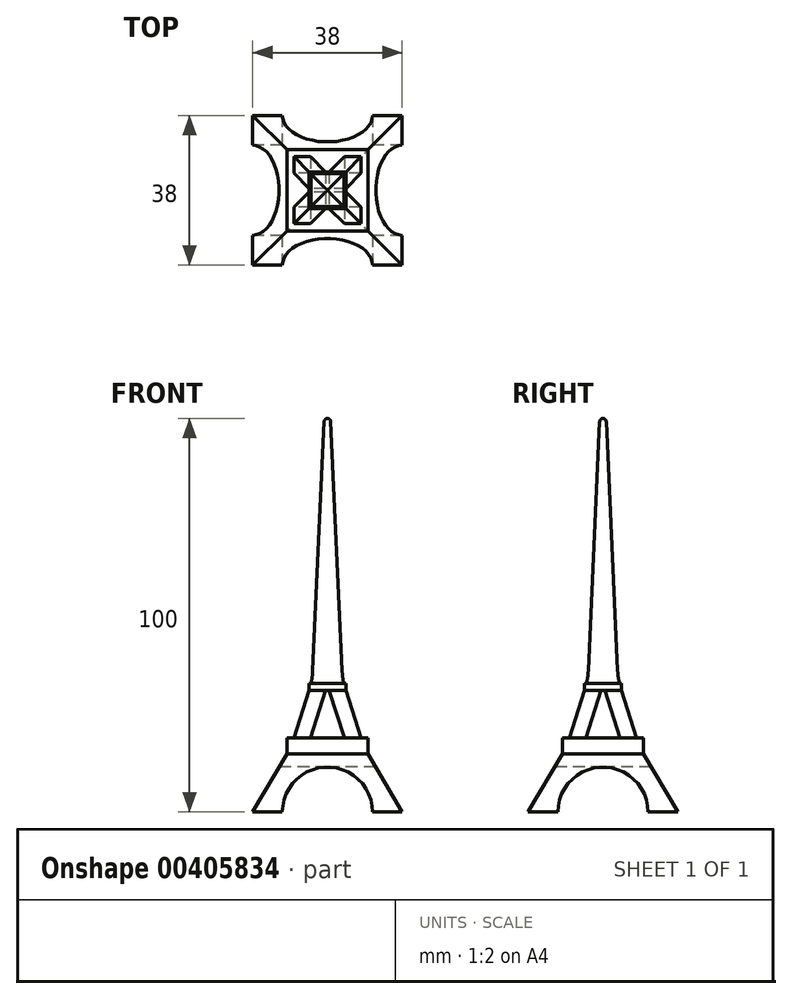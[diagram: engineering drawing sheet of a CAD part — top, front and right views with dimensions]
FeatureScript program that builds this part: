
annotation { "Feature Type Name" : "Feature", "Feature Type Description" : "" }
export const myFeature = defineFeature(function(context is Context, id is Id, definition is map)
    precondition{}
    {
        {
            var Q0;
            Q0=qCreatedBy(makeId("Front.planeOp"),FACE);
            var sketch = newSketch(context, id + "F0", { "sketchPlane" : qUnion([Q0])});
            skLineSegment(sketch, "E0.bottom", {"start": v(0, 0) * mm, "end": v(38, 0) * mm});
            skLineSegment(sketch, "E0.top", {"start": v(0, 100) * mm, "end": v(38, 100) * mm});
            skLineSegment(sketch, "E0.left", {"start": v(0, 0) * mm, "end": v(0, 100) * mm});
            skLineSegment(sketch, "E0.right", {"start": v(38, 0) * mm, "end": v(38, 100) * mm});
            skSolve(sketch);
        }
        {
            var Q0;
            Q0=makeQuery(id+"F0.imprint","IMPRINT",FACE,{"disambiguationData":[TD([[makeQuery(id+"F0.imprint","IMPRINT",EDGE,{"derivedFrom":sQuery(id+"F0.wireOp",EDGE,"E0.bottom")}),1.0]])]});
            extrude(context, id + "F1", {"entities" : qUnion([Q0]), "depth" : 38 * mm});
        }
        {
            var Q0;
            Q0=makeQuery(id+"F1.opExtrude","CAP_FACE",FACE,{"disambiguationData":[OSD([sQuery(id+"F0.wireOp",EDGE,"E0.bottom"),sQuery(id+"F0.wireOp",EDGE,"E0.top"),sQuery(id+"F0.wireOp",EDGE,"E0.left"),sQuery(id+"F0.wireOp",EDGE,"E0.right")])],"isStart":false});
            var sketch = newSketch(context, id + "F2", { "sketchPlane" : qUnion([Q0])});
            skPoint(sketch, "E1.endSnap0", {"position": v(19, 100) * mm});
            skLineSegment(sketch, "E2", {"start": v(19, 100) * mm, "end": v(19, 0) * mm, "construction": true});
            skLineSegment(sketch, "E3", {"start": v(19, 100) * mm, "end": v(19.03, 100) * mm});
            skLineSegment(sketch, "E4", {"start": v(19.83, 99.24) * mm, "end": v(22.72, 36.04) * mm});
            skLineSegment(sketch, "E5", {"start": v(38, 0) * mm, "end": v(29.32, 14.77) * mm});
            skLineSegment(sketch, "E6", {"start": v(27.53, 18.8) * mm, "end": v(23.66, 30.85) * mm});
            skArc(sketch, "E7", {"start": v(30.49, 0) * mm, "mid": v(27.12, 8.12) * mm, "end": v(19, 11.49) * mm});
            skLineSegment(sketch, "E8", {"start": v(38, 0) * mm, "end": v(30.49, 0) * mm});
            skPoint(sketch, "E9.visualSharp", {"position": v(22.85, 33.38) * mm});
            skArc(sketch, "E9.filletArc", {"start": v(22.72, 36.04) * mm, "mid": v(22.88, 34.33) * mm, "end": v(23.17, 32.64) * mm});
            skPoint(sketch, "E10.visualSharp", {"position": v(28.2, 16.68) * mm});
            skLineSegment(sketch, "E11.MirrorCS", {"start": v(18.17, 99.24) * mm, "end": v(15.28, 36.04) * mm});
            skArc(sketch, "E12.MirrorCS", {"start": v(15.28, 36.04) * mm, "mid": v(15.12, 34.33) * mm, "end": v(14.83, 32.64) * mm});
            skLineSegment(sketch, "E13.MirrorCS", {"start": v(10.47, 18.8) * mm, "end": v(14.34, 30.85) * mm});
            skLineSegment(sketch, "E14.MirrorCS", {"start": v(19, 100) * mm, "end": v(18.97, 100) * mm});
            skLineSegment(sketch, "E15.MirrorCS", {"start": v(0, 0) * mm, "end": v(8.68, 14.77) * mm});
            skArc(sketch, "E16.MirrorCS", {"start": v(7.51, 0) * mm, "mid": v(10.88, 8.12) * mm, "end": v(19, 11.49) * mm});
            skLineSegment(sketch, "E17.MirrorCS", {"start": v(0, 0) * mm, "end": v(7.51, 0) * mm});
            skLineSegment(sketch, "E18.bottom", {"start": v(-8.57, -4.89) * mm, "end": v(50.47, -4.89) * mm});
            skLineSegment(sketch, "E18.top", {"start": v(-8.57, 109.12) * mm, "end": v(50.47, 109.12) * mm});
            skLineSegment(sketch, "E18.left", {"start": v(-8.57, -4.89) * mm, "end": v(-8.57, 109.12) * mm});
            skLineSegment(sketch, "E18.right", {"start": v(50.47, -4.89) * mm, "end": v(50.47, 109.12) * mm});
            skLineSegment(sketch, "E19", {"start": v(29.32, 14.77) * mm, "end": v(29.32, 18.8) * mm});
            skLineSegment(sketch, "E20", {"start": v(29.32, 18.8) * mm, "end": v(27.53, 18.8) * mm});
            skLineSegment(sketch, "E21.MirrorCS", {"start": v(8.68, 18.8) * mm, "end": v(10.47, 18.8) * mm});
            skLineSegment(sketch, "E22.MirrorCS", {"start": v(8.68, 14.77) * mm, "end": v(8.68, 18.8) * mm});
            skLineSegment(sketch, "E23", {"start": v(23.66, 30.85) * mm, "end": v(23.66, 32.64) * mm});
            skLineSegment(sketch, "E24", {"start": v(23.66, 32.64) * mm, "end": v(23.17, 32.64) * mm});
            skLineSegment(sketch, "E25.MirrorCS", {"start": v(14.34, 30.85) * mm, "end": v(14.34, 32.64) * mm});
            skLineSegment(sketch, "E26.MirrorCS", {"start": v(14.34, 32.64) * mm, "end": v(14.83, 32.64) * mm});
            skPoint(sketch, "E27.orphan", {"position": v(14.34, 30.85) * mm});
            skPoint(sketch, "E28.visualSharp", {"position": v(18.2, 100) * mm});
            skArc(sketch, "E28.filletArc", {"start": v(18.97, 100) * mm, "mid": v(18.42, 99.78) * mm, "end": v(18.17, 99.24) * mm});
            skPoint(sketch, "E29.visualSharp", {"position": v(19.8, 100) * mm});
            skArc(sketch, "E29.filletArc", {"start": v(19.83, 99.24) * mm, "mid": v(19.58, 99.78) * mm, "end": v(19.03, 100) * mm});
            skLineSegment(sketch, "E30.0", {"start": v(14.67, 18.8) * mm, "end": v(18.54, 30.85) * mm});
            skLineSegment(sketch, "E31.0", {"start": v(23.33, 18.8) * mm, "end": v(19.46, 30.85) * mm});
            skLineSegment(sketch, "E32", {"start": v(23.33, 18.8) * mm, "end": v(14.67, 18.8) * mm});
            skLineSegment(sketch, "E33", {"start": v(19.46, 30.85) * mm, "end": v(18.54, 30.85) * mm});
            skSolve(sketch);
        }
        {
            var Q0;
            {var subQ2=sQuery(id+"F2.wireOp",EDGE,"E11.MirrorCS");Q0=makeQuery(id+"F2.imprint","IMPRINT",FACE,{"disambiguationData":[TD([[makeQuery(id+"F2.imprint","IMPRINT",EDGE,{"derivedFrom":subQ2}),-1.0]])]});}
            var Q1;
            {var subQ0=sQuery(id+"F2.wireOp",EDGE,"E7");Q1=makeQuery(id+"F2.imprint","IMPRINT",FACE,{"disambiguationData":[TD([[makeQuery(id+"F2.imprint","IMPRINT",EDGE,{"derivedFrom":subQ0}),1.0]])]});}
            var Q2;
            {var subQ2=sQuery(id+"F2.wireOp",EDGE,"E4");Q2=makeQuery(id+"F2.imprint","IMPRINT",FACE,{"disambiguationData":[TD([[makeQuery(id+"F2.imprint","IMPRINT",EDGE,{"derivedFrom":subQ2}),1.0]])]});}
            var Q3;
            Q3=makeQuery(id+"F2.imprint","IMPRINT",FACE,{"disambiguationData":[TD([[makeQuery(id+"F2.imprint","IMPRINT",EDGE,{"derivedFrom":sQuery(id+"F2.wireOp",EDGE,"E30.0")}),-1.0]])]});
            extrude(context, id + "F3", {"entities" : qUnion([Q0, Q1, Q2, Q3]), "operationType" : NewBodyOperationType.REMOVE, "endBound" : BoundingType.THROUGH_ALL, "oppositeDirection" : true, "depth" : 25 * mm});
        }
        {
            var Q0;
            Q0=qCreatedBy(makeId("Right.planeOp"),FACE);
            var sketch = newSketch(context, id + "F4", { "sketchPlane" : qUnion([Q0])});
            skPoint(sketch, "E34.endSnap0", {"position": v(-19, 100) * mm});
            skLineSegment(sketch, "E35", {"start": v(-19, 100) * mm, "end": v(-19, 0) * mm, "construction": true});
            skLineSegment(sketch, "E36", {"start": v(-19, 100) * mm, "end": v(-18.97, 100) * mm});
            skLineSegment(sketch, "E37", {"start": v(-18.17, 99.24) * mm, "end": v(-15.28, 36.04) * mm});
            skLineSegment(sketch, "E38", {"start": v(0, 0) * mm, "end": v(-8.68, 14.77) * mm});
            skLineSegment(sketch, "E39", {"start": v(-10.47, 18.8) * mm, "end": v(-14.34, 30.85) * mm});
            skArc(sketch, "E40", {"start": v(-7.51, 0) * mm, "mid": v(-10.88, 8.12) * mm, "end": v(-19, 11.49) * mm});
            skLineSegment(sketch, "E41", {"start": v(0, 0) * mm, "end": v(-7.51, 0) * mm});
            skPoint(sketch, "E42.visualSharp", {"position": v(-15.15, 33.38) * mm});
            skArc(sketch, "E42.filletArc", {"start": v(-15.28, 36.04) * mm, "mid": v(-15.12, 34.33) * mm, "end": v(-14.83, 32.64) * mm});
            skPoint(sketch, "E43.visualSharp", {"position": v(-9.8, 16.68) * mm});
            skLineSegment(sketch, "E44.MirrorCS", {"start": v(-19.83, 99.24) * mm, "end": v(-22.72, 36.04) * mm});
            skArc(sketch, "E45.MirrorCS", {"start": v(-22.72, 36.04) * mm, "mid": v(-22.88, 34.33) * mm, "end": v(-23.17, 32.64) * mm});
            skLineSegment(sketch, "E46.MirrorCS", {"start": v(-27.53, 18.8) * mm, "end": v(-23.66, 30.85) * mm});
            skLineSegment(sketch, "E47.MirrorCS", {"start": v(-19, 100) * mm, "end": v(-19.03, 100) * mm});
            skLineSegment(sketch, "E48.MirrorCS", {"start": v(-38, 0) * mm, "end": v(-29.32, 14.77) * mm});
            skArc(sketch, "E49.MirrorCS", {"start": v(-30.49, 0) * mm, "mid": v(-27.12, 8.12) * mm, "end": v(-19, 11.49) * mm});
            skLineSegment(sketch, "E50.MirrorCS", {"start": v(-38, 0) * mm, "end": v(-30.49, 0) * mm});
            skLineSegment(sketch, "E51.bottom", {"start": v(-46.57, -4.89) * mm, "end": v(12.47, -4.89) * mm});
            skLineSegment(sketch, "E51.top", {"start": v(-46.57, 109.12) * mm, "end": v(12.47, 109.12) * mm});
            skLineSegment(sketch, "E51.left", {"start": v(-46.57, -4.89) * mm, "end": v(-46.57, 109.12) * mm});
            skLineSegment(sketch, "E51.right", {"start": v(12.47, -4.89) * mm, "end": v(12.47, 109.12) * mm});
            skLineSegment(sketch, "E52", {"start": v(-8.68, 14.77) * mm, "end": v(-8.68, 18.8) * mm});
            skLineSegment(sketch, "E53", {"start": v(-8.68, 18.8) * mm, "end": v(-10.47, 18.8) * mm});
            skLineSegment(sketch, "E54.MirrorCS", {"start": v(-29.32, 18.8) * mm, "end": v(-27.53, 18.8) * mm});
            skLineSegment(sketch, "E55.MirrorCS", {"start": v(-29.32, 14.77) * mm, "end": v(-29.32, 18.8) * mm});
            skLineSegment(sketch, "E56", {"start": v(-14.34, 30.85) * mm, "end": v(-14.34, 32.64) * mm});
            skLineSegment(sketch, "E57", {"start": v(-14.34, 32.64) * mm, "end": v(-14.83, 32.64) * mm});
            skLineSegment(sketch, "E58.MirrorCS", {"start": v(-23.66, 30.85) * mm, "end": v(-23.66, 32.64) * mm});
            skLineSegment(sketch, "E59.MirrorCS", {"start": v(-23.66, 32.64) * mm, "end": v(-23.17, 32.64) * mm});
            skPoint(sketch, "E60.MirrorCS.center.orphan", {"position": v(-46.57, 24.9) * mm});
            skPoint(sketch, "E60.MirrorCS.start.orphan", {"position": v(-27.53, 18.8) * mm});
            skPoint(sketch, "E61.orphan", {"position": v(-23.66, 30.85) * mm});
            skLineSegment(sketch, "E62.0", {"start": v(-23.33, 18.8) * mm, "end": v(-19.46, 30.85) * mm});
            skLineSegment(sketch, "E63.0", {"start": v(-14.67, 18.8) * mm, "end": v(-18.54, 30.85) * mm});
            skLineSegment(sketch, "E64", {"start": v(-14.67, 18.8) * mm, "end": v(-23.33, 18.8) * mm});
            skLineSegment(sketch, "E65", {"start": v(-14.34, 30.85) * mm, "end": v(-23.66, 30.85) * mm});
            skPoint(sketch, "E66.visualSharp", {"position": v(-19.8, 100) * mm});
            skArc(sketch, "E66.filletArc", {"start": v(-19.03, 100) * mm, "mid": v(-19.58, 99.78) * mm, "end": v(-19.83, 99.24) * mm});
            skPoint(sketch, "E67.visualSharp", {"position": v(-18.2, 100) * mm});
            skArc(sketch, "E67.filletArc", {"start": v(-18.17, 99.24) * mm, "mid": v(-18.42, 99.78) * mm, "end": v(-18.97, 100) * mm});
            skSolve(sketch);
        }
        {
            var Q0;
            Q0=makeQuery(id+"F4.imprint","IMPRINT",FACE,{"disambiguationData":[TD([[makeQuery(id+"F4.imprint","IMPRINT",EDGE,{"derivedFrom":sQuery(id+"F4.wireOp",EDGE,"E36")}),1.0]])]});
            var Q1;
            Q1=makeQuery(id+"F4.imprint","IMPRINT",FACE,{"disambiguationData":[TD([[makeQuery(id+"F4.imprint","IMPRINT",EDGE,{"derivedFrom":sQuery(id+"F4.wireOp",EDGE,"E62.0")}),-1.0]])]});
            extrude(context, id + "F5", {"entities" : qUnion([Q0, Q1]), "operationType" : NewBodyOperationType.REMOVE, "endBound" : BoundingType.THROUGH_ALL, "depth" : 25 * mm});
        }
    });
